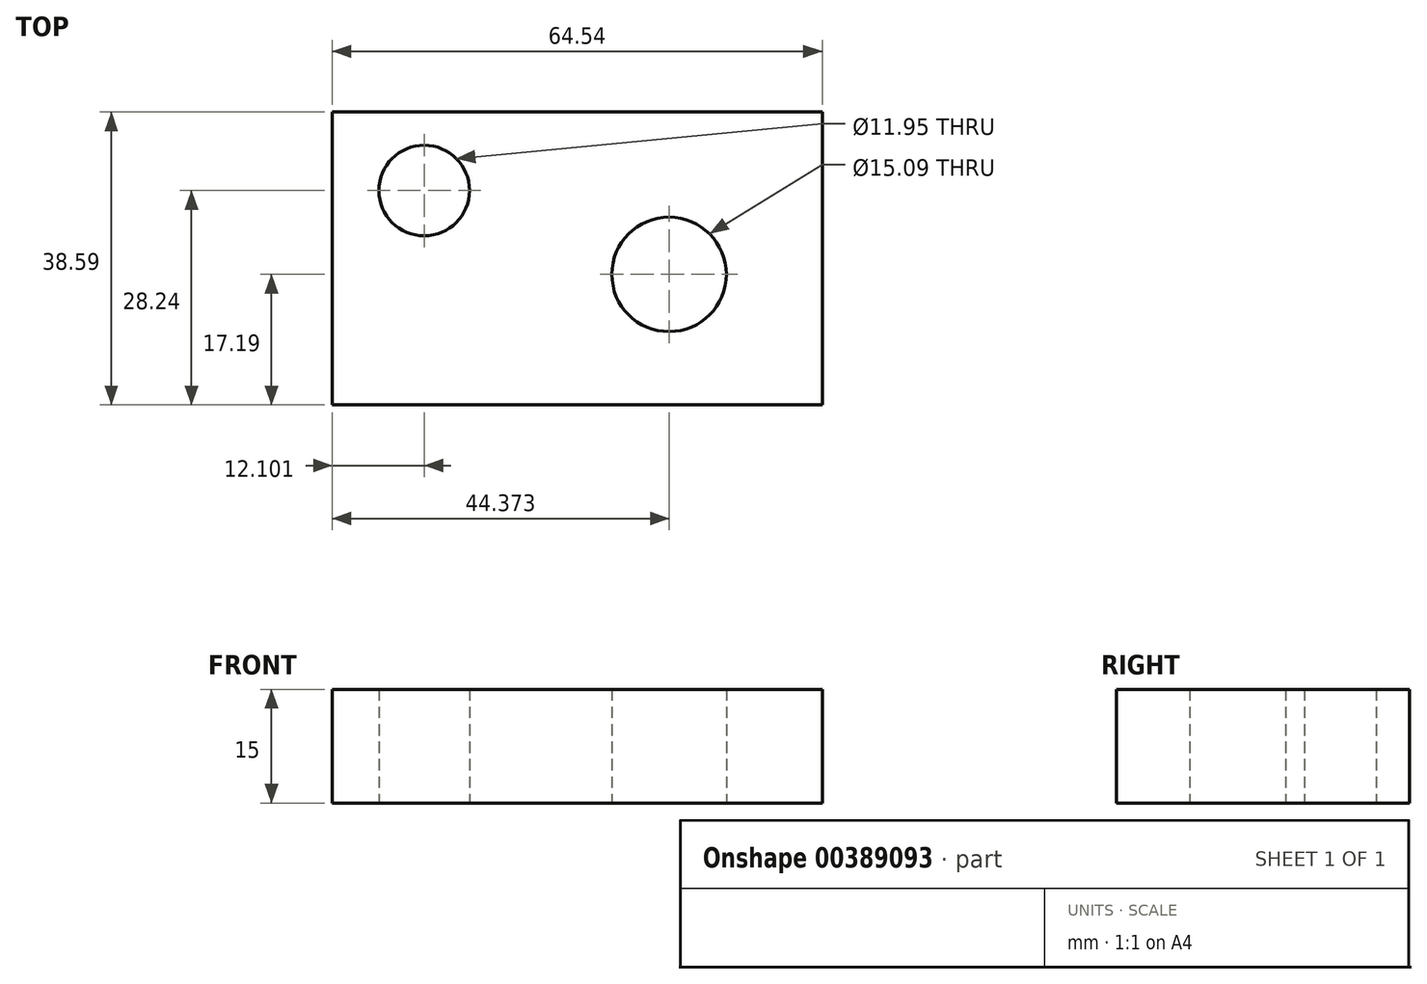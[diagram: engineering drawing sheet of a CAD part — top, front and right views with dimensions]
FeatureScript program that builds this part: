
annotation { "Feature Type Name" : "Feature", "Feature Type Description" : "" }
export const myFeature = defineFeature(function(context is Context, id is Id, definition is map)
    precondition{}
    {
        {
            var Q0;
            Q0=qCreatedBy(makeId("Top.planeOp"),FACE);
            var sketch = newSketch(context, id + "F0", { "sketchPlane" : qUnion([Q0])});
            skLineSegment(sketch, "E0.bottom", {"start": v(-28.5, 21.4) * mm, "end": v(36.04, 21.4) * mm});
            skLineSegment(sketch, "E0.top", {"start": v(-28.5, -17.19) * mm, "end": v(36.04, -17.19) * mm});
            skLineSegment(sketch, "E0.left", {"start": v(-28.5, 21.4) * mm, "end": v(-28.5, -17.19) * mm});
            skLineSegment(sketch, "E0.right", {"start": v(36.04, 21.4) * mm, "end": v(36.04, -17.19) * mm});
            skCircle(sketch, "E1", {"center": v(-16.4, 11.05) * mm, "radius": 5.97 * mm});
            skCircle(sketch, "E2", {"center": v(15.87, 0) * mm, "radius": 7.54 * mm});
            skSolve(sketch);
        }
        {
            var Q0;
            Q0=makeQuery(id+"F0.imprint","IMPRINT",FACE,{"disambiguationData":[TD([[makeQuery(id+"F0.imprint","IMPRINT",EDGE,{"derivedFrom":sQuery(id+"F0.wireOp",EDGE,"E0.bottom")}),-1.0]])]});
            extrude(context, id + "F1", {"entities" : qUnion([Q0]), "depth" : 15 * mm});
        }
    });
